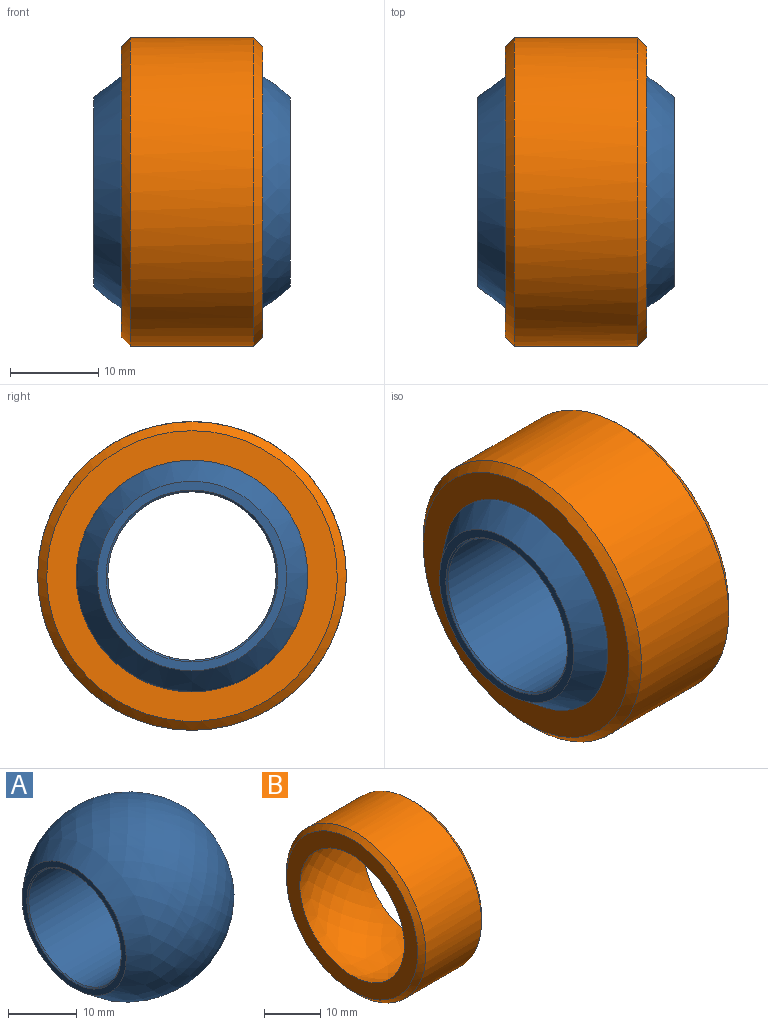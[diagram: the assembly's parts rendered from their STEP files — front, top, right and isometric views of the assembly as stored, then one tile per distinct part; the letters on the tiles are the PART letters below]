
ASSEMBLY  parts=2 mates=1
PART A: 6 faces, bbox 22.2x30.5x30.5 mm
  f0: plane 21.46x21.46mm, normal (-1,0,0), area 64.6mm2, adj f3,f4
  f1: cylinder r=9.53mm len=21.82mm, axis (1,0,0), area 1305.9mm2, adj f4,f5
  f2: plane 21.46x21.46mm, normal (1,0,0), area 64.6mm2, adj f3,f5
  f3: revolved ~30.53x30.53mm, area 2122.1mm2, adj f0,f2
  f4: cone r=9.72mm half-angle=45deg, axis (-1,0,0), area 17.1mm2, adj f0,f1
  f5: cone r=9.53mm half-angle=45deg, axis (1,0,0), area 17.1mm2, adj f1,f2
PART B: 6 faces, bbox 16x34.9x34.9 mm
  f0: cylinder r=17.46mm len=34.93mm, axis (1,0,0), area 1531.7mm2, adj f4,f5
  f1: plane 32.89x32.89mm, normal (-1,0,0), area 309.6mm2, adj f2,f4
  f2: revolved ~30.54x30.54mm, area 1532.2mm2, adj f1,f3
  f3: plane 32.89x32.89mm, normal (1,0,0), area 309.6mm2, adj f2,f5
  f4: cone r=17.46mm half-angle=45deg, axis (1,0,0), area 153.6mm2, adj f0,f1
  f5: cone r=16.44mm half-angle=45deg, axis (-1,0,0), area 153.6mm2, adj f0,f3
PLACE A t=(3.88,7.68,0.92)mm
PLACE B t=(3.88,7.68,0.92)mm
MATE ball B.f0 <-> A.f1  axis (1,0,0) through (3.88,7.68,0.92)mm
